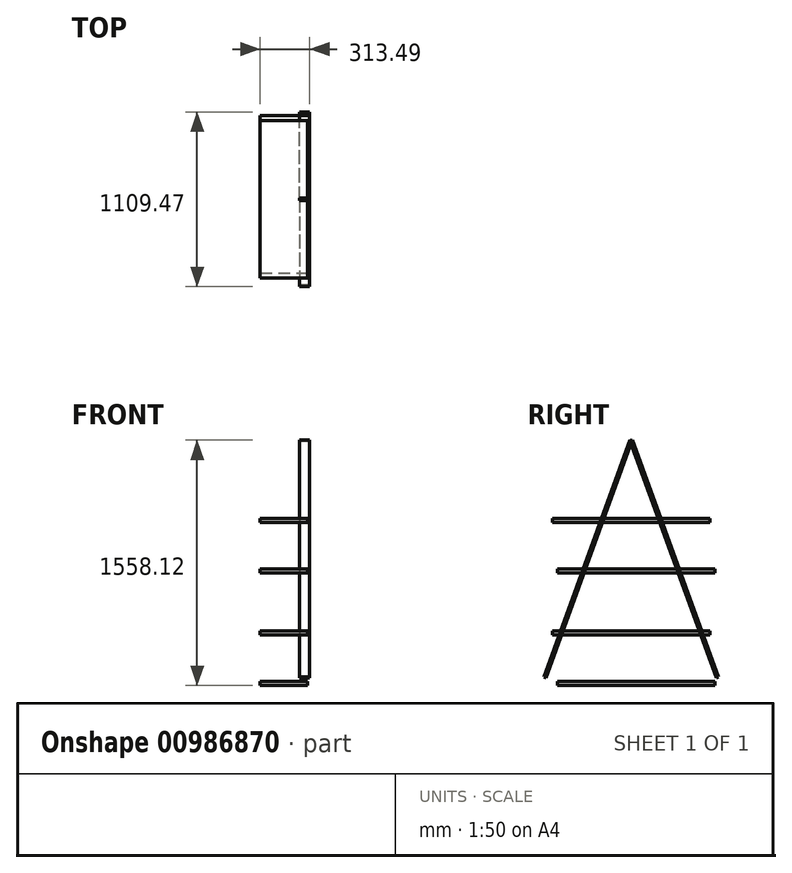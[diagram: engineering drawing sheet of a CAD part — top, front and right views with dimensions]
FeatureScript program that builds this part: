
annotation { "Feature Type Name" : "Feature", "Feature Type Description" : "" }
export const myFeature = defineFeature(function(context is Context, id is Id, definition is map)
    precondition{}
    {
        {
            var Q0;
            Q0=qCreatedBy(makeId("Front.planeOp"),FACE);
            var sketch = newSketch(context, id + "F0", { "sketchPlane" : qUnion([Q0])});
            skLineSegment(sketch, "E0.bottom", {"start": v(-51.5, 1553) * mm, "end": v(13.5, 1553) * mm});
            skLineSegment(sketch, "E0.top", {"start": v(-51.5, -47) * mm, "end": v(13.5, -47) * mm});
            skLineSegment(sketch, "E0.left", {"start": v(-51.5, 1553) * mm, "end": v(-51.5, -47) * mm});
            skLineSegment(sketch, "E0.right", {"start": v(13.5, 1553) * mm, "end": v(13.5, -47) * mm});
            skSolve(sketch);
        }
        {
            var Q0;
            Q0=makeQuery(id+"F0.imprint","IMPRINT",FACE,{"disambiguationData":[TD([[makeQuery(id+"F0.imprint","IMPRINT",EDGE,{"derivedFrom":sQuery(id+"F0.wireOp",EDGE,"E0.bottom")}),-1.0]])]});
            extrude(context, id + "F1", {"entities" : qUnion([Q0]), "depth" : 15 * mm, "offsetDistance" : 25 * mm});
        }
        {
            var Q0;
            Q0=makeQuery(id+"F1.opExtrude","SWEPT_BODY",BODY,{"disambiguationData":[OSD([sQuery(id+"F0.wireOp",EDGE,"E0.bottom"),sQuery(id+"F0.wireOp",EDGE,"E0.top"),sQuery(id+"F0.wireOp",EDGE,"E0.left"),sQuery(id+"F0.wireOp",EDGE,"E0.right")])]});
            var Q1;
            Q1=makeQuery(id+"F1.opExtrude","CAP_EDGE",EDGE,{"disambiguationData":[OSD([sQuery(id+"F0.wireOp",EDGE,"E0.bottom")])],"isStart":true});
            transform(context, id + "F2", {"entities" : qUnion([Q0]), "transformType" : TransformType.ROTATION, "transformAxis" : qUnion([Q1]), "angle" : 20 * degree, "oppositeDirection" : true, "makeCopy" : true});
        }
        {
            var Q0;
            Q0=makeQuery(id+"F1.opExtrude","SWEPT_BODY",BODY,{"disambiguationData":[OSD([sQuery(id+"F0.wireOp",EDGE,"E0.bottom"),sQuery(id+"F0.wireOp",EDGE,"E0.top"),sQuery(id+"F0.wireOp",EDGE,"E0.left"),sQuery(id+"F0.wireOp",EDGE,"E0.right")])]});
            var Q1;
            Q1=makeQuery(id+"F1.opExtrude","CAP_EDGE",EDGE,{"disambiguationData":[OSD([sQuery(id+"F0.wireOp",EDGE,"E0.top")])],"isStart":false});
            var Q2;
            Q2=makeQuery(id+"F2.opPattern","COPY",EDGE,{"derivedFrom":makeQuery(id+"F1.opExtrude","CAP_EDGE",EDGE,{"disambiguationData":[OSD([sQuery(id+"F0.wireOp",EDGE,"E0.bottom")])],"isStart":false}),"instanceName":"1"});
            transform(context, id + "F3", {"entities" : qUnion([Q0]), "transformType" : TransformType.ROTATION, "transformAxis" : qUnion([Q2]), "angle" : 20 * degree, "makeCopy" : false});
        }
        {
            var Q0;
            Q0=qCreatedBy(makeId("Top.planeOp"),FACE);
            var sketch = newSketch(context, id + "F4", { "sketchPlane" : qUnion([Q0])});
            skLineSegment(sketch, "E1.bottom", {"start": v(-300, -472.82) * mm, "end": v(0, -472.82) * mm});
            skLineSegment(sketch, "E1.top", {"start": v(-300, 527.18) * mm, "end": v(0, 527.18) * mm});
            skLineSegment(sketch, "E1.left", {"start": v(-300, -472.82) * mm, "end": v(-300, 527.18) * mm});
            skLineSegment(sketch, "E1.right", {"start": v(0, -472.82) * mm, "end": v(0, 527.18) * mm});
            skSolve(sketch);
        }
        {
            var Q0;
            Q0 = qSketchRegion(id + "F4", true);
            extrude(context, id + "F5", {"entities" : qUnion([Q0]), "depth" : 25 * mm, "offsetDistance" : 25 * mm});
        }
        {
            var Q0;
            Q0=makeQuery(id+"F5.opExtrude","SWEPT_BODY",BODY,{"disambiguationData":[OSD([sQuery(id+"F4.wireOp",EDGE,"E1.bottom"),sQuery(id+"F4.wireOp",EDGE,"E1.top"),sQuery(id+"F4.wireOp",EDGE,"E1.left"),sQuery(id+"F4.wireOp",EDGE,"E1.right")])]});
            var Q1;
            Q1=makeQuery(id+"F5.opExtrude","CAP_FACE",FACE,{"disambiguationData":[OSD([sQuery(id+"F4.wireOp",EDGE,"E1.bottom"),sQuery(id+"F4.wireOp",EDGE,"E1.top"),sQuery(id+"F4.wireOp",EDGE,"E1.left"),sQuery(id+"F4.wireOp",EDGE,"E1.right")])],"isStart":false});
            transform(context, id + "F6", {"entities" : qUnion([Q0]), "transformType" : TransformType.TRANSLATION_3D, "dx" : 0 * mm, "dy" : -34 * mm, "dz" : 322 * mm, "makeCopy" : true});
        }
        {
            var Q0;
            Q0=makeQuery(id+"F5.opExtrude","SWEPT_BODY",BODY,{"disambiguationData":[OSD([sQuery(id+"F4.wireOp",EDGE,"E1.bottom"),sQuery(id+"F4.wireOp",EDGE,"E1.top"),sQuery(id+"F4.wireOp",EDGE,"E1.left"),sQuery(id+"F4.wireOp",EDGE,"E1.right")])]});
            var Q1;
            Q1=makeQuery(id+"F6.opPattern","COPY",BODY,{"derivedFrom":makeQuery(id+"F5.opExtrude","SWEPT_BODY",BODY,{"disambiguationData":[OSD([sQuery(id+"F4.wireOp",EDGE,"E1.bottom"),sQuery(id+"F4.wireOp",EDGE,"E1.top"),sQuery(id+"F4.wireOp",EDGE,"E1.left"),sQuery(id+"F4.wireOp",EDGE,"E1.right")])]}),"instanceName":"1"});
            transform(context, id + "F7", {"entities" : qUnion([Q0, Q1]), "transformType" : TransformType.TRANSLATION_3D, "dx" : 0 * mm, "dy" : 0 * mm, "dz" : 715 * mm, "makeCopy" : true});
        }
    });
